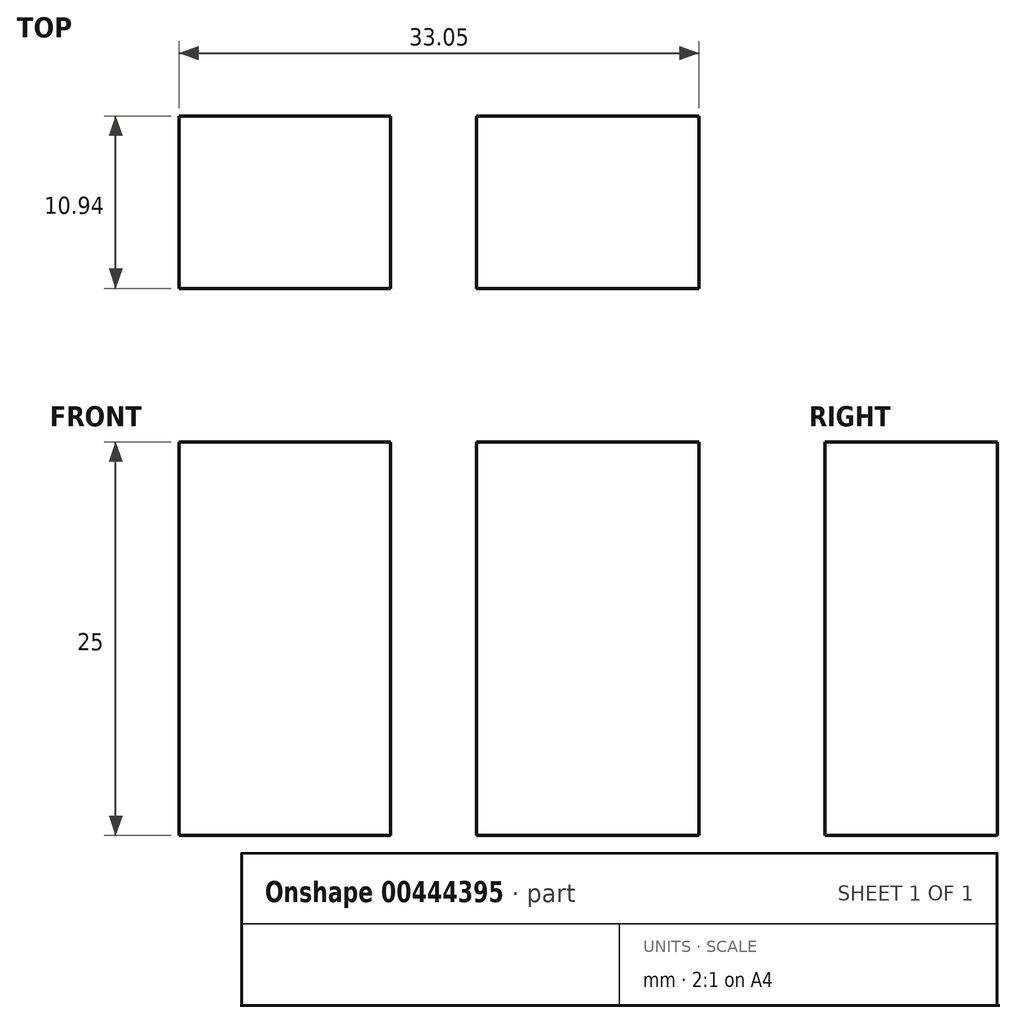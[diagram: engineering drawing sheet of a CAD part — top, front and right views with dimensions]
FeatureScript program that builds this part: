
annotation { "Feature Type Name" : "Feature", "Feature Type Description" : "" }
export const myFeature = defineFeature(function(context is Context, id is Id, definition is map)
    precondition{}
    {
        {
            var Q0;
            Q0=qCreatedBy(makeId("Top.planeOp"),FACE);
            var sketch = newSketch(context, id + "F0", { "sketchPlane" : qUnion([Q0])});
            skLineSegment(sketch, "E0.bottom", {"start": v(-33.05, 29.1) * mm, "end": v(-19.6, 29.1) * mm});
            skLineSegment(sketch, "E0.top", {"start": v(-33.05, 18.16) * mm, "end": v(-19.6, 18.16) * mm});
            skLineSegment(sketch, "E0.left", {"start": v(-33.05, 29.1) * mm, "end": v(-33.05, 18.16) * mm});
            skLineSegment(sketch, "E0.right", {"start": v(-19.6, 29.1) * mm, "end": v(-19.6, 18.16) * mm});
            skLineSegment(sketch, "E1.bottom", {"start": v(-14.13, 29.1) * mm, "end": v(0, 29.1) * mm});
            skLineSegment(sketch, "E1.top", {"start": v(-14.13, 18.16) * mm, "end": v(0, 18.16) * mm});
            skLineSegment(sketch, "E1.left", {"start": v(-14.13, 29.1) * mm, "end": v(-14.13, 18.16) * mm});
            skLineSegment(sketch, "E1.right", {"start": v(0, 29.1) * mm, "end": v(0, 18.16) * mm});
            skSolve(sketch);
        }
        {
            var Q0;
            Q0 = qSketchRegion(id + "F0", true);
            extrude(context, id + "F1", {"entities" : qUnion([Q0]), "depth" : 25 * mm});
        }
    });
